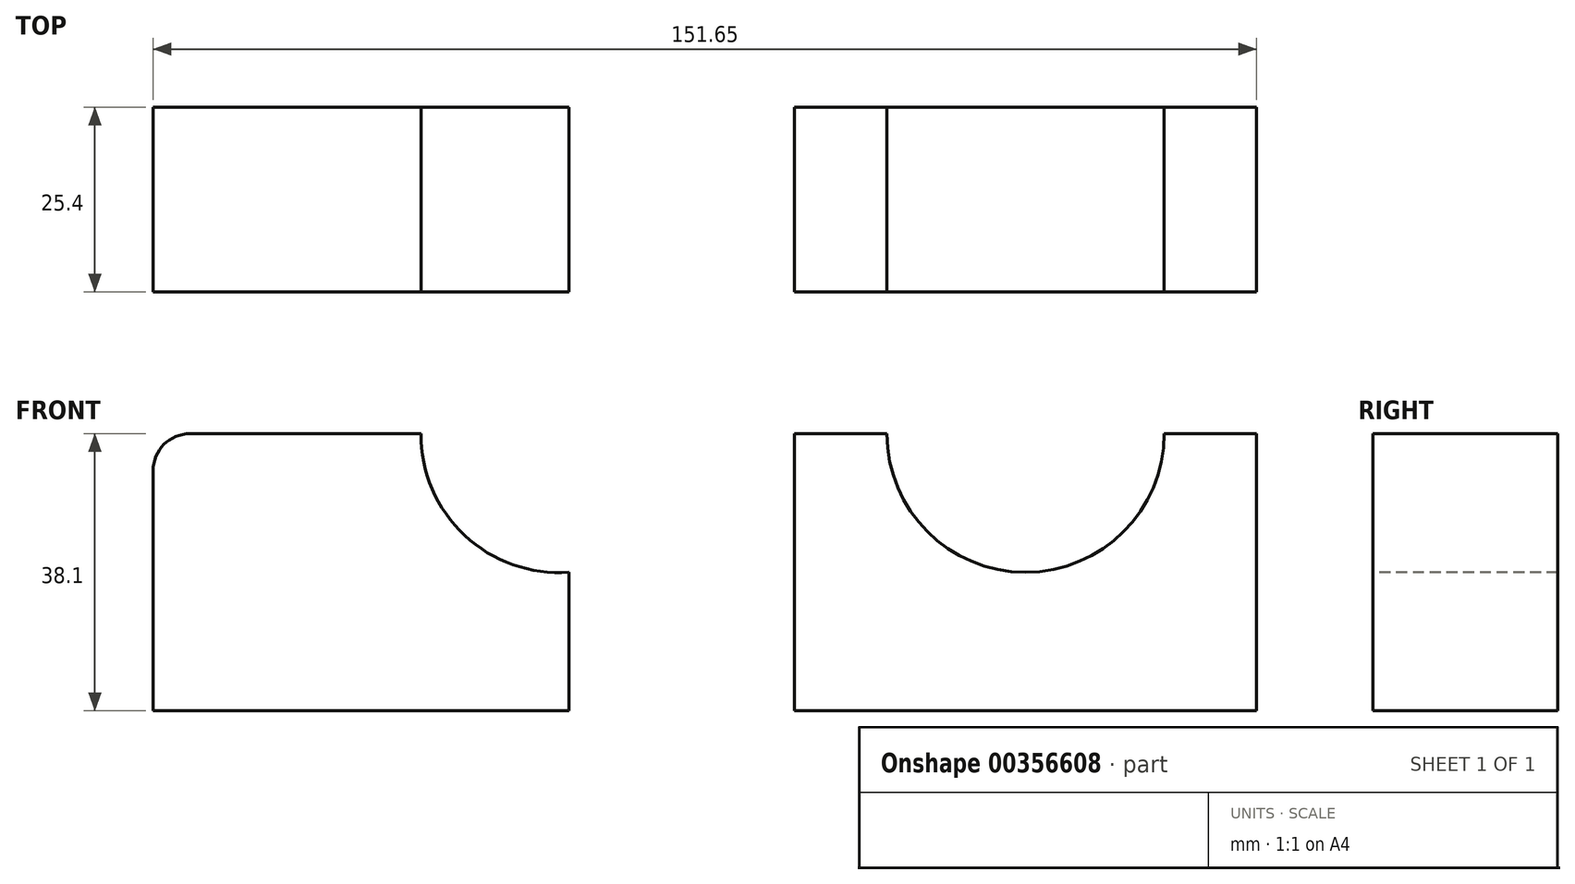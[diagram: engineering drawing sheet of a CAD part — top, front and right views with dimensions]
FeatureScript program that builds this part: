
annotation { "Feature Type Name" : "Feature", "Feature Type Description" : "" }
export const myFeature = defineFeature(function(context is Context, id is Id, definition is map)
    precondition{}
    {
        {
            var Q0;
            Q0=qCreatedBy(makeId("Front.planeOp"),FACE);
            var sketch = newSketch(context, id + "F0", { "sketchPlane" : qUnion([Q0])});
            skLineSegment(sketch, "E0.bottom", {"start": v(-82.17, 0) * mm, "end": v(-25.02, 0) * mm});
            skLineSegment(sketch, "E0.top", {"start": v(-82.17, 38.1) * mm, "end": v(-25.02, 38.1) * mm});
            skLineSegment(sketch, "E0.left", {"start": v(-82.17, 0) * mm, "end": v(-82.17, 38.1) * mm});
            skLineSegment(sketch, "E0.right", {"start": v(-25.02, 0) * mm, "end": v(-25.02, 38.1) * mm});
            skSolve(sketch);
        }
        {
            var Q0;
            Q0 = qSketchRegion(id + "F0", true);
            extrude(context, id + "F1", {"entities" : qUnion([Q0]), "depth" : 25.4 * mm});
        }
        {
            var Q0;
            Q0=makeQuery(id+"F1.opExtrude","SWEPT_EDGE",EDGE,{"disambiguationData":[OSD([sQuery(id+"F0.wireOp",EDGE,"E0.top"),sQuery(id+"F0.wireOp",EDGE,"E0.left")])]});
            fillet(context, id + "F2", {"entities" : qUnion([Q0]), "radius" : 5.08 * mm, "tangentPropagation" : true, "allowEdgeOverflow" : false});
        }
        {
            var Q0;
            Q0=qCreatedBy(makeId("Front.planeOp"),FACE);
            var sketch = newSketch(context, id + "F3", { "sketchPlane" : qUnion([Q0])});
            skLineSegment(sketch, "E1.bottom", {"start": v(5.98, 0) * mm, "end": v(69.48, 0) * mm});
            skLineSegment(sketch, "E1.top", {"start": v(5.98, 38.1) * mm, "end": v(69.48, 38.1) * mm});
            skLineSegment(sketch, "E1.left", {"start": v(5.98, 0) * mm, "end": v(5.98, 38.1) * mm});
            skLineSegment(sketch, "E1.right", {"start": v(69.48, 0) * mm, "end": v(69.48, 38.1) * mm});
            skSolve(sketch);
        }
        {
            var Q0;
            Q0 = qSketchRegion(id + "F3", true);
            extrude(context, id + "F4", {"entities" : qUnion([Q0]), "depth" : 25.4 * mm});
        }
        {
            var Q0;
            Q0=makeQuery(id+"F4.opExtrude","CAP_FACE",FACE,{"disambiguationData":[OSD([sQuery(id+"F3.wireOp",EDGE,"E1.bottom"),sQuery(id+"F3.wireOp",EDGE,"E1.top"),sQuery(id+"F3.wireOp",EDGE,"E1.left"),sQuery(id+"F3.wireOp",EDGE,"E1.right")])],"isStart":false});
            var sketch = newSketch(context, id + "F5", { "sketchPlane" : qUnion([Q0])});
            skCircle(sketch, "E2", {"center": v(37.73, 38.1) * mm, "radius": 19.05 * mm});
            skSolve(sketch);
        }
        {
            var Q0;
            Q0 = qSketchRegion(id + "F5", true);
            extrude(context, id + "F6", {"entities" : qUnion([Q0]), "operationType" : NewBodyOperationType.REMOVE, "oppositeDirection" : true, "depth" : 25.4 * mm});
        }
        {
            var Q0;
            Q0=makeQuery(id+"F1.opExtrude","CAP_FACE",FACE,{"disambiguationData":[OSD([sQuery(id+"F0.wireOp",EDGE,"E0.bottom"),sQuery(id+"F0.wireOp",EDGE,"E0.top"),sQuery(id+"F0.wireOp",EDGE,"E0.left"),sQuery(id+"F0.wireOp",EDGE,"E0.right")])],"isStart":false});
            var sketch = newSketch(context, id + "F7", { "sketchPlane" : qUnion([Q0])});
            skPoint(sketch, "E3", {"position": v(-45.34, 38.1) * mm});
            skPoint(sketch, "E4", {"position": v(-25.02, 19.05) * mm});
            skArc(sketch, "E5", {"start": v(-45.34, 38.1) * mm, "mid": v(-39.35, 24.12) * mm, "end": v(-25.02, 19.05) * mm});
            skSolve(sketch);
        }
        {
            var Q0;
            Q0 = qSketchRegion(id + "F7", true);
            var Q1;
            {var subQ0=sQuery(id+"F7.wireOp",EDGE,"E5");Q1=makeQuery(id+"F7.imprint","IMPRINT",FACE,{"disambiguationData":[TD([[makeQuery(id+"F7.imprint","IMPRINT",EDGE,{"derivedFrom":subQ0}),1.0]])]});}
            extrude(context, id + "F8", {"entities" : qUnion([Q0, Q1]), "operationType" : NewBodyOperationType.REMOVE, "oppositeDirection" : true, "depth" : 25.4 * mm});
        }
    });
